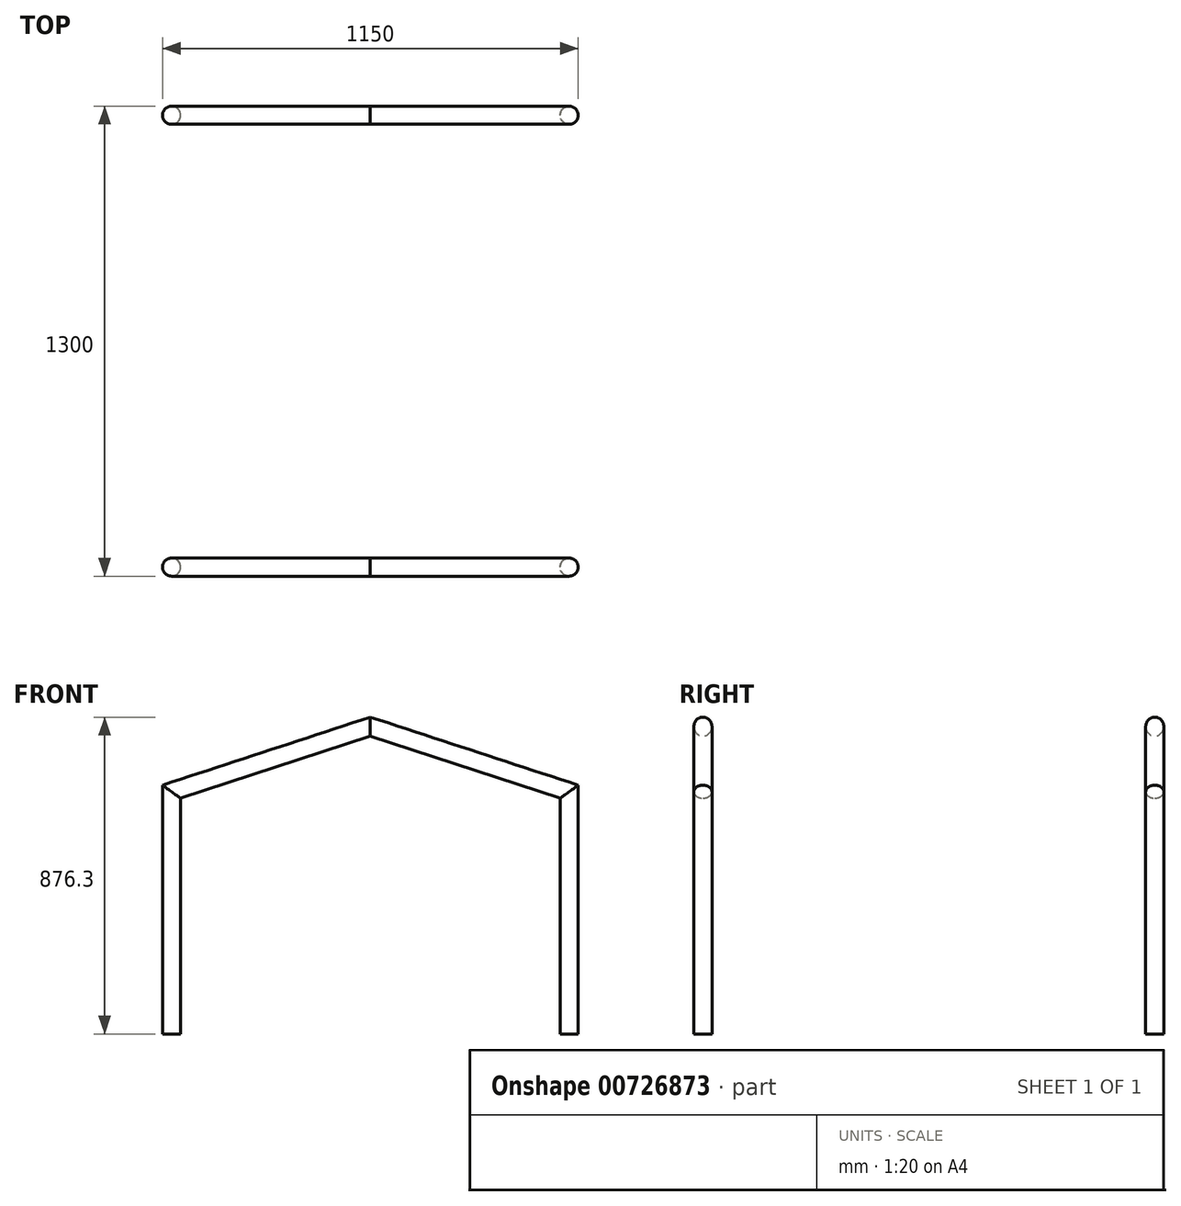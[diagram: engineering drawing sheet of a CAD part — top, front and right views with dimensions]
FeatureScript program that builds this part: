
annotation { "Feature Type Name" : "Feature", "Feature Type Description" : "" }
export const myFeature = defineFeature(function(context is Context, id is Id, definition is map)
    precondition{}
    {
        {
            var Q0;
            Q0=qCreatedBy(makeId("Front.planeOp"),FACE);
            var sketch = newSketch(context, id + "F0", { "sketchPlane" : qUnion([Q0])});
            skLineSegment(sketch, "E0", {"start": v(0, 0) * mm, "end": v(0, 670) * mm});
            skLineSegment(sketch, "E1", {"start": v(550, 850) * mm, "end": v(0, 670) * mm});
            skLineSegment(sketch, "E2", {"start": v(550, 850) * mm, "end": v(1100, 670) * mm});
            skLineSegment(sketch, "E3", {"start": v(1100, 670) * mm, "end": v(1100, 0) * mm});
            skPoint(sketch, "E4.start.orphan", {"position": v(550, 670) * mm});
            skCircle(sketch, "E5", {"center": v(0, 670) * mm, "radius": 25 * mm});
            skCircle(sketch, "E6", {"center": v(550, 850) * mm, "radius": 25 * mm});
            skCircle(sketch, "E7", {"center": v(1100, 670) * mm, "radius": 25 * mm});
            skCircle(sketch, "E8", {"center": v(0, 0) * mm, "radius": 25 * mm});
            skCircle(sketch, "E9", {"center": v(1100, 0) * mm, "radius": 25 * mm});
            skSolve(sketch);
        }
        {
            var Q0;
            Q0=qCreatedBy(makeId("Top.planeOp"),FACE);
            var sketch = newSketch(context, id + "F1", { "sketchPlane" : qUnion([Q0])});
            skCircle(sketch, "E10", {"center": v(0, 0) * mm, "radius": 25 * mm});
            skSolve(sketch);
        }
        {
            var Q0;
            Q0=qCreatedBy(makeId("Front.planeOp"),FACE);
            cPlane(context, id + "F2", {"entities" : qUnion([Q0]), "cplaneType" : CPlaneType.OFFSET, "offset" : 2500 * mm, "width" : 150 * mm, "height" : 150 * mm});
        }
        {
            var Q0;
            Q0=qCreatedBy(id+"F2.planeOp",FACE);
            var sketch = newSketch(context, id + "F3", { "sketchPlane" : qUnion([Q0])});
            skLineSegment(sketch, "E11", {"start": v(0, 0) * mm, "end": v(0, 670) * mm});
            skLineSegment(sketch, "E12", {"start": v(550, 850) * mm, "end": v(0, 670) * mm});
            skLineSegment(sketch, "E13", {"start": v(1100, 670) * mm, "end": v(550, 850) * mm});
            skLineSegment(sketch, "E14", {"start": v(1100, 670) * mm, "end": v(1100, 0) * mm});
            skPoint(sketch, "E15.start.orphan", {"position": v(550, 670) * mm});
            skCircle(sketch, "E16", {"center": v(0, 670) * mm, "radius": 25 * mm});
            skCircle(sketch, "E17", {"center": v(550, 850) * mm, "radius": 25 * mm});
            skCircle(sketch, "E18", {"center": v(1100, 670) * mm, "radius": 25 * mm});
            skCircle(sketch, "E19", {"center": v(0, 0) * mm, "radius": 25 * mm});
            skCircle(sketch, "E20", {"center": v(1100, 0) * mm, "radius": 25 * mm});
            skSolve(sketch);
        }
        {
            var Q0;
            Q0=qCreatedBy(id+"F2.planeOp",FACE);
            cPlane(context, id + "F4", {"entities" : qUnion([Q0]), "cplaneType" : CPlaneType.OFFSET, "offset" : 1250 * mm, "oppositeDirection" : true, "width" : 150 * mm, "height" : 150 * mm});
        }
        {
            var Q0;
            Q0=qCreatedBy(id+"F4.planeOp",FACE);
            var sketch = newSketch(context, id + "F5", { "sketchPlane" : qUnion([Q0])});
            skLineSegment(sketch, "E21", {"start": v(0, 0) * mm, "end": v(0, 670) * mm});
            skLineSegment(sketch, "E22", {"start": v(1100, 670) * mm, "end": v(1100, 0) * mm});
            skLineSegment(sketch, "E23", {"start": v(550, 850) * mm, "end": v(0, 670) * mm});
            skLineSegment(sketch, "E24", {"start": v(1100, 670) * mm, "end": v(550, 850) * mm});
            skPoint(sketch, "E25.start.orphan", {"position": v(550, 670) * mm});
            skCircle(sketch, "E26", {"center": v(0, 670) * mm, "radius": 25 * mm});
            skCircle(sketch, "E27", {"center": v(550, 850) * mm, "radius": 25 * mm});
            skCircle(sketch, "E28", {"center": v(1100, 670) * mm, "radius": 25 * mm});
            skCircle(sketch, "E29", {"center": v(0, 0) * mm, "radius": 25 * mm});
            skCircle(sketch, "E30", {"center": v(1100, 0) * mm, "radius": 25 * mm});
            skSolve(sketch);
        }
        {
            var Q0;
            Q0=qCreatedBy(makeId("Right.planeOp"),FACE);
            var sketch = newSketch(context, id + "F6", { "sketchPlane" : qUnion([Q0])});
            skLineSegment(sketch, "E31", {"start": v(0, 0) * mm, "end": v(-2500, 0) * mm});
            skLineSegment(sketch, "E32", {"start": v(-2500, 670) * mm, "end": v(0, 670) * mm});
            skSolve(sketch);
        }
        {
            var Q0;
            Q0=qCreatedBy(makeId("Top.planeOp"),FACE);
            var Q1;
            Q1=sQuery(id+"F0.wireOp",VERTEX,"E1.start");
            cPlane(context, id + "F7", {"entities" : qUnion([Q0, Q1]), "cplaneType" : CPlaneType.PLANE_POINT, "offset" : 25 * mm, "width" : 150 * mm, "height" : 150 * mm});
        }
        {
            var Q0;
            Q0=qCreatedBy(id+"F7.planeOp",FACE);
            var Q1;
            Q1=sQuery(id+"F0.wireOp",VERTEX,"E2.end");
            cPlane(context, id + "F8", {"entities" : qUnion([Q0, Q1]), "cplaneType" : CPlaneType.PLANE_POINT, "offset" : 25 * mm, "width" : 150 * mm, "height" : 150 * mm});
        }
        {
            var Q0;
            Q0=qCreatedBy(id+"F8.planeOp",FACE);
            cPlane(context, id + "F9", {"entities" : qUnion([Q0]), "cplaneType" : CPlaneType.OFFSET, "offset" : 670 * mm, "oppositeDirection" : true, "width" : 150 * mm, "height" : 150 * mm});
        }
        {
            var Q0;
            Q0=makeQuery(id+"F1.imprint","IMPRINT",FACE,{"disambiguationData":[TD([[makeQuery(id+"F1.imprint","IMPRINT",EDGE,{"derivedFrom":sQuery(id+"F1.wireOp",EDGE,"E10")}),1.0]])]});
            var Q1;
            Q1=sQuery(id+"F0.wireOp",EDGE,"E1");
            var Q2;
            Q2=sQuery(id+"F0.wireOp",EDGE,"E2");
            var Q3;
            Q3=sQuery(id+"F0.wireOp",EDGE,"E0");
            var Q4;
            Q4=sQuery(id+"F0.wireOp",EDGE,"E3");
            sweep(context, id + "F10", {"profiles" : qUnion([Q0]), "path" : qUnion([Q1, Q2, Q3, Q4])});
        }
        {
            var Q0;
            Q0=qCreatedBy(makeId("Top.planeOp"),FACE);
            var Q1;
            Q1=sQuery(id+"F3.wireOp",VERTEX,"E11.start");
            cPlane(context, id + "F11", {"entities" : qUnion([Q0, Q1]), "cplaneType" : CPlaneType.PLANE_POINT, "offset" : 25 * mm, "width" : 150 * mm, "height" : 150 * mm});
        }
        {
            var Q0;
            Q0=qCreatedBy(id+"F11.planeOp",FACE);
            var sketch = newSketch(context, id + "F12", { "sketchPlane" : qUnion([Q0])});
            skLineSegment(sketch, "E33", {"start": v(0, 0) * mm, "end": v(0, -2500) * mm});
            skLineSegment(sketch, "E34", {"start": v(0, 0) * mm, "end": v(0, -1250) * mm});
            skCircle(sketch, "E35", {"center": v(0, -1250) * mm, "radius": 25 * mm});
            skCircle(sketch, "E36", {"center": v(0, -2500) * mm, "radius": 25 * mm});
            skSolve(sketch);
        }
        {
            var Q0;
            {var subQ0=sQuery(id+"F12.wireOp",EDGE,"E34");var subQ1=sQuery(id+"F12.wireOp",EDGE,"E33");var subQ2=makeQuery(id+"F12.imprint","INTERSECT",VERTEX,{"derivedFrom":[subQ1,subQ0]});Q0=makeQuery(id+"F12.imprint","IMPRINT",FACE,{"disambiguationData":[TD([[makeQuery(id+"F12.imprint","IMPRINT",EDGE,{"disambiguationData":[TD([[subQ2,-1.0]])],"derivedFrom":subQ1}),1.0]])]});}
            var Q1;
            {var subQ0=sQuery(id+"F12.wireOp",EDGE,"E34");var subQ1=sQuery(id+"F12.wireOp",EDGE,"E33");var subQ2=makeQuery(id+"F12.imprint","INTERSECT",VERTEX,{"derivedFrom":[subQ1,subQ0]});Q1=makeQuery(id+"F12.imprint","IMPRINT",FACE,{"disambiguationData":[TD([[makeQuery(id+"F12.imprint","IMPRINT",EDGE,{"disambiguationData":[TD([[subQ2,-1.0]])],"derivedFrom":subQ1}),-1.0]])]});}
            var Q2;
            Q2=sQuery(id+"F5.wireOp",EDGE,"E21");
            var Q3;
            Q3=sQuery(id+"F5.wireOp",EDGE,"E23");
            var Q4;
            Q4=sQuery(id+"F5.wireOp",EDGE,"E24");
            var Q5;
            Q5=sQuery(id+"F5.wireOp",EDGE,"E22");
            sweep(context, id + "F13", {"profiles" : qUnion([Q0, Q1]), "path" : qUnion([Q2, Q3, Q4, Q5])});
        }
    });
